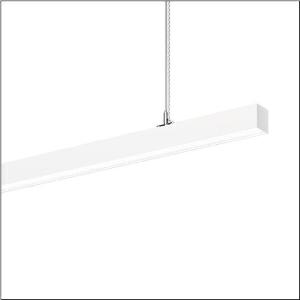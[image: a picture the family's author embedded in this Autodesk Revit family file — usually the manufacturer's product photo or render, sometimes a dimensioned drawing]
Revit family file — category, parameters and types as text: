
# Revit family: silica_r__21_51mx33db49wb_5808
name_source: partatom
category: Lighting Fixtures
units: mm (PartAtom-declared; Revit-internal decimal feet)

## family parameters
Cut with Voids When Loaded = No
Host = Face
Light Source = No
Part Type = Normal
Room Calculation Point = No
Round Connector Dimension = Use Diameter
Shared = No

## types (1)
- --- (1 x LED, 7390 lm, 48.3 W, 4000K)
    Apparent Load = 48 VA
    CIE Flux Codes = 78 96 99 55 100
    Color Rendering = 80
    Color Temperature = 4000K
    Default Elevation = 1800 mm
    Description = Silica® 21, office luminaire, primary optical cover: prismatic diffuser, of PMMA, CAT 2 (L<= 3000cd/m²), light emission: direct/indirect distribution, primary light characteristic: symmetric, installation type: suspended mounting, LED, rated luminous flux: 7.390lm, luminous efficacy: 153lm/W, light colour: 840, colour temperature: 4000K, with terminal, 3+2-pole, max. 2.5mm², mains connection: 220..240V, AC, 50/60Hz, rated input power: 48.3W, luminaire housing, of aluminium, traffic white (RAL 9016), length: 1.504mm, width: 53mm, height: 53mm, protection rating (complete): IP20, insulation class (complete): insulation class I (protective earthing), certification: CE, permissible operating ambient temperature: 0..+35°C, standard: EN 50419, packaging unit: 1 piece
    Height = 53 mm
    Lamp = 1 x LED
    Lamp Light Flux = 7390 lm
    Lamp Power = 48.3 W
    Lamp count = 1
    Length = 1504 mm
    Luminous efficacy = 153 lm/W
    Manufacturer = Siteco
    ModVariant = No
    Model = 51MX33DB49WB
    Mounting Place = Ceiling
    Mounting Type = Pendant
    Number of Poles = 1
    OnlyDefault = Yes
    Power Factor = 1
    Product Name = Silica® 21
    Product group = office luminaire | ceiling pendant
    ProductGroupID = 902
    Protection Class = Protection class I
    Protection Degree = IP 20
    RLX_Detail_Level = 1
    RLX_Emergency_Light_Flux = 0 lm
    RLX_Emergency_Type = 0
    RLX_Emergency_Type_DB = No
    RlxData = <blob elided: 21601 chars, md5=5b6b3f6a>
    Socket = socket
    Standby Power = 0 W
    System Light Flux = 7390 lm
    System Power = 48 W
    Type Comments = factory setting: luminous flux: 100 % | dim-lin: 254 | 323 mA
    Type Image = l_1335916.jpg
    URL = http://relux.com
    VarID = @adj_087377
    Voltage = 0 V
    Weight = 0.00 kg
    Width = 53 mm

## geometry (parser evidence)
native form markers: Blend x4, Sweep x13
no freeform markers — native parametric forms only
